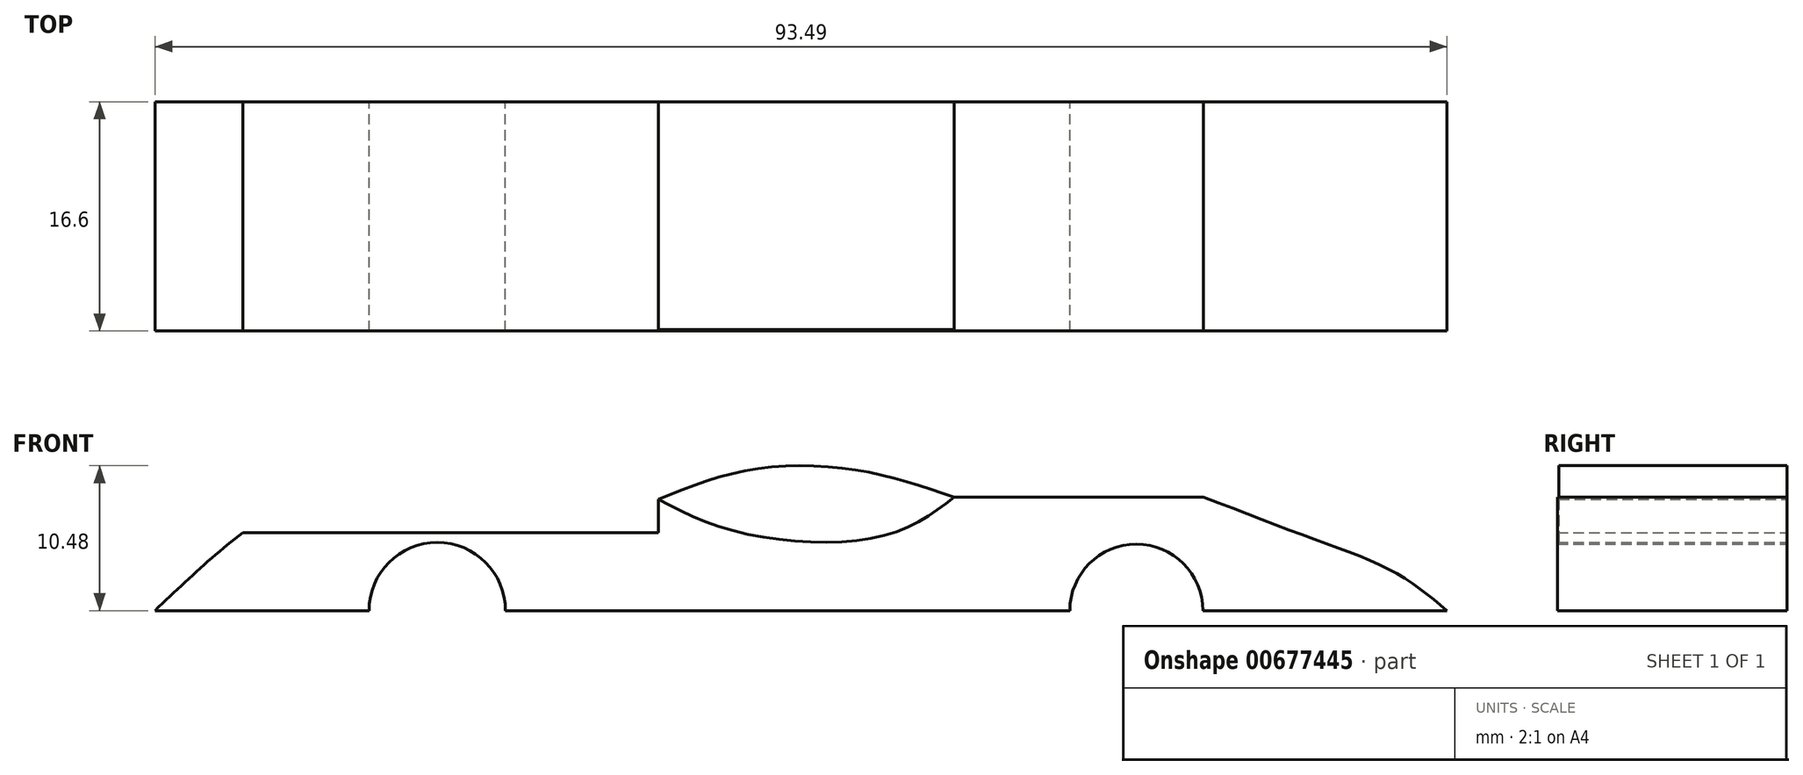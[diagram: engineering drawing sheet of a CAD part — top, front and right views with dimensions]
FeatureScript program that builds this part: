
annotation { "Feature Type Name" : "Feature", "Feature Type Description" : "" }
export const myFeature = defineFeature(function(context is Context, id is Id, definition is map)
    precondition{}
    {
        {
            var Q0;
            Q0=qCreatedBy(makeId("Front.planeOp"),FACE);
            var sketch = newSketch(context, id + "F0", { "sketchPlane" : qUnion([Q0])});
            skFitSpline(sketch, "E0", {"points": [v(-44.32, 0) * mm, v(-32.49, 8.83) * mm, v(-20.08, 10.57) * mm, v(-12.12, 10.18) * mm, v(-4.17, 6.3) * mm, v(9.4, 5.72) * mm, v(15.61, 9.6) * mm, v(24.15, 10.38) * mm, v(37.53, 5.92) * mm, v(45.3, 2.81) * mm, v(49.17, 0) * mm], "startDerivative": vector(91.31, 87.06) * mm, "endDerivative": vector(50.63, -42.53) * mm});
            skLineSegment(sketch, "E1", {"start": v(-44.32, 0) * mm, "end": v(49.17, 0) * mm});
            skSolve(sketch);
        }
        {
            var Q0;
            Q0 = qSketchRegion(id + "F0", true);
            extrude(context, id + "F1", {"entities" : qUnion([Q0]), "endBound" : BoundingType.SYMMETRIC, "depth" : 16.6 * mm, "offsetDistance" : 25 * mm});
        }
        {
            var Q0;
            Q0=makeQuery(id+"F1.opExtrude","CAP_FACE",FACE,{"disambiguationData":[OSD([sQuery(id+"F0.wireOp",EDGE,"E0"),sQuery(id+"F0.wireOp",EDGE,"E1")])],"isStart":true});
            var sketch = newSketch(context, id + "F2", { "sketchPlane" : qUnion([Q0])});
            skFitSpline(sketch, "E2", {"points": [v(-13.51, 8.2) * mm, v(-6.97, 10.07) * mm, v(1.12, 10.21) * mm, v(7.88, 8.06) * mm], "startDerivative": vector(19.49, 6.73) * mm, "endDerivative": vector(19.76, -7.97) * mm});
            skSolve(sketch);
        }
        {
            var Q0;
            Q0=makeQuery(id+"F1.opExtrude","CAP_FACE",FACE,{"disambiguationData":[OSD([sQuery(id+"F0.wireOp",EDGE,"E0"),sQuery(id+"F0.wireOp",EDGE,"E1")])],"isStart":false});
            var sketch = newSketch(context, id + "F3", { "sketchPlane" : qUnion([Q0])});
            skFitSpline(sketch, "E3", {"points": [v(-7.82, 8.03) * mm, v(-1.08, 10.27) * mm, v(7.05, 10.1) * mm, v(13.54, 8.23) * mm], "startDerivative": vector(19.67, 8.35) * mm, "endDerivative": vector(19.36, -6.71) * mm});
            skSolve(sketch);
        }
        {
            var Q0;
            Q0 = qSketchRegion(id + "F3", true);
            var Q1;
            {var subQ0=sQuery(id+"F2.wireOp",EDGE,"E2");Q1=makeQuery(id+"F2.imprint","IMPRINT",FACE,{"disambiguationData":[TD([[makeQuery(id+"F2.imprint","IMPRINT",EDGE,{"derivedFrom":subQ0}),-1.0]])]});}
            extrude(context, id + "F4", {"entities" : qUnion([Q0, Q1]), "operationType" : NewBodyOperationType.ADD, "oppositeDirection" : true, "depth" : 16.5 * mm, "offsetDistance" : 25 * mm});
        }
        {
            var Q0;
            {var subQ0=sQuery(id+"F0.wireOp",EDGE,"E0");Q0=makeQuery(id+"F4.boolean.opBoolean","MERGE",FACE,{"derivedFrom":[makeQuery(id+"F1.opExtrude","CAP_FACE",FACE,{"disambiguationData":[OSD([subQ0,sQuery(id+"F0.wireOp",EDGE,"E1")])],"isStart":true}),makeQuery(id+"F4.opExtrude","CAP_FACE",FACE,{"disambiguationData":[OSD([subQ0,sQuery(id+"F2.wireOp",EDGE,"E2")])],"isStart":true})]});}
            var sketch = newSketch(context, id + "F5", { "sketchPlane" : qUnion([Q0])});
            skLineSegment(sketch, "E4.bottom", {"start": v(7.88, 20.19) * mm, "end": v(47.72, 20.19) * mm});
            skLineSegment(sketch, "E4.top", {"start": v(7.88, 5.65) * mm, "end": v(47.72, 5.65) * mm});
            skLineSegment(sketch, "E4.left", {"start": v(7.88, 20.19) * mm, "end": v(7.88, 5.65) * mm});
            skLineSegment(sketch, "E4.right", {"start": v(47.72, 20.19) * mm, "end": v(47.72, 5.65) * mm});
            skSolve(sketch);
        }
        {
            var Q0;
            Q0 = qSketchRegion(id + "F5", true);
            extrude(context, id + "F6", {"entities" : qUnion([Q0]), "operationType" : NewBodyOperationType.REMOVE, "oppositeDirection" : true, "depth" : 27.5 * mm, "offsetDistance" : 25 * mm});
        }
        {
            var Q0;
            {var subQ0=sQuery(id+"F0.wireOp",EDGE,"E0");Q0=makeQuery(id+"F4.boolean.opBoolean","MERGE",FACE,{"derivedFrom":[makeQuery(id+"F1.opExtrude","CAP_FACE",FACE,{"disambiguationData":[OSD([subQ0,sQuery(id+"F0.wireOp",EDGE,"E1")])],"isStart":true}),makeQuery(id+"F4.opExtrude","CAP_FACE",FACE,{"disambiguationData":[OSD([subQ0,sQuery(id+"F2.wireOp",EDGE,"E2")])],"isStart":true})]});}
            var sketch = newSketch(context, id + "F7", { "sketchPlane" : qUnion([Q0])});
            skLineSegment(sketch, "E5.bottom", {"start": v(-13.51, 8.2) * mm, "end": v(-46.84, 8.2) * mm});
            skLineSegment(sketch, "E5.top", {"start": v(-13.51, 26.86) * mm, "end": v(-46.84, 26.86) * mm});
            skLineSegment(sketch, "E5.left", {"start": v(-13.51, 8.2) * mm, "end": v(-13.51, 26.86) * mm});
            skLineSegment(sketch, "E5.right", {"start": v(-46.84, 8.2) * mm, "end": v(-46.84, 26.86) * mm});
            skSolve(sketch);
        }
        {
            var Q0;
            Q0 = qSketchRegion(id + "F7", true);
            extrude(context, id + "F8", {"entities" : qUnion([Q0]), "operationType" : NewBodyOperationType.REMOVE, "oppositeDirection" : true, "depth" : 25 * mm, "offsetDistance" : 25 * mm});
        }
        {
            var Q0;
            {var subQ0=sQuery(id+"F0.wireOp",EDGE,"E0");Q0=makeQuery(id+"F4.boolean.opBoolean","MERGE",FACE,{"derivedFrom":[makeQuery(id+"F1.opExtrude","CAP_FACE",FACE,{"disambiguationData":[OSD([subQ0,sQuery(id+"F0.wireOp",EDGE,"E1")])],"isStart":true}),makeQuery(id+"F4.opExtrude","CAP_FACE",FACE,{"disambiguationData":[OSD([subQ0,sQuery(id+"F2.wireOp",EDGE,"E2")])],"isStart":true})]});}
            var sketch = newSketch(context, id + "F9", { "sketchPlane" : qUnion([Q0])});
            skCircle(sketch, "E6", {"center": v(-26.7, 0) * mm, "radius": 4.8 * mm});
            skSolve(sketch);
        }
        {
            var Q0;
            Q0 = qSketchRegion(id + "F9", true);
            extrude(context, id + "F10", {"entities" : qUnion([Q0]), "operationType" : NewBodyOperationType.REMOVE, "oppositeDirection" : true, "depth" : 25 * mm, "offsetDistance" : 25 * mm});
        }
        {
            var Q0;
            {var subQ0=sQuery(id+"F0.wireOp",EDGE,"E0");Q0=makeQuery(id+"F4.boolean.opBoolean","MERGE",FACE,{"derivedFrom":[makeQuery(id+"F1.opExtrude","CAP_FACE",FACE,{"disambiguationData":[OSD([subQ0,sQuery(id+"F0.wireOp",EDGE,"E1")])],"isStart":true}),makeQuery(id+"F4.opExtrude","CAP_FACE",FACE,{"disambiguationData":[OSD([subQ0,sQuery(id+"F2.wireOp",EDGE,"E2")])],"isStart":true})]});}
            var sketch = newSketch(context, id + "F11", { "sketchPlane" : qUnion([Q0])});
            skCircle(sketch, "E7", {"center": v(23.89, 0) * mm, "radius": 4.93 * mm});
            skSolve(sketch);
        }
        {
            var Q0;
            Q0 = qSketchRegion(id + "F11", true);
            extrude(context, id + "F12", {"entities" : qUnion([Q0]), "operationType" : NewBodyOperationType.REMOVE, "oppositeDirection" : true, "depth" : 25 * mm, "offsetDistance" : 25 * mm});
        }
    });
